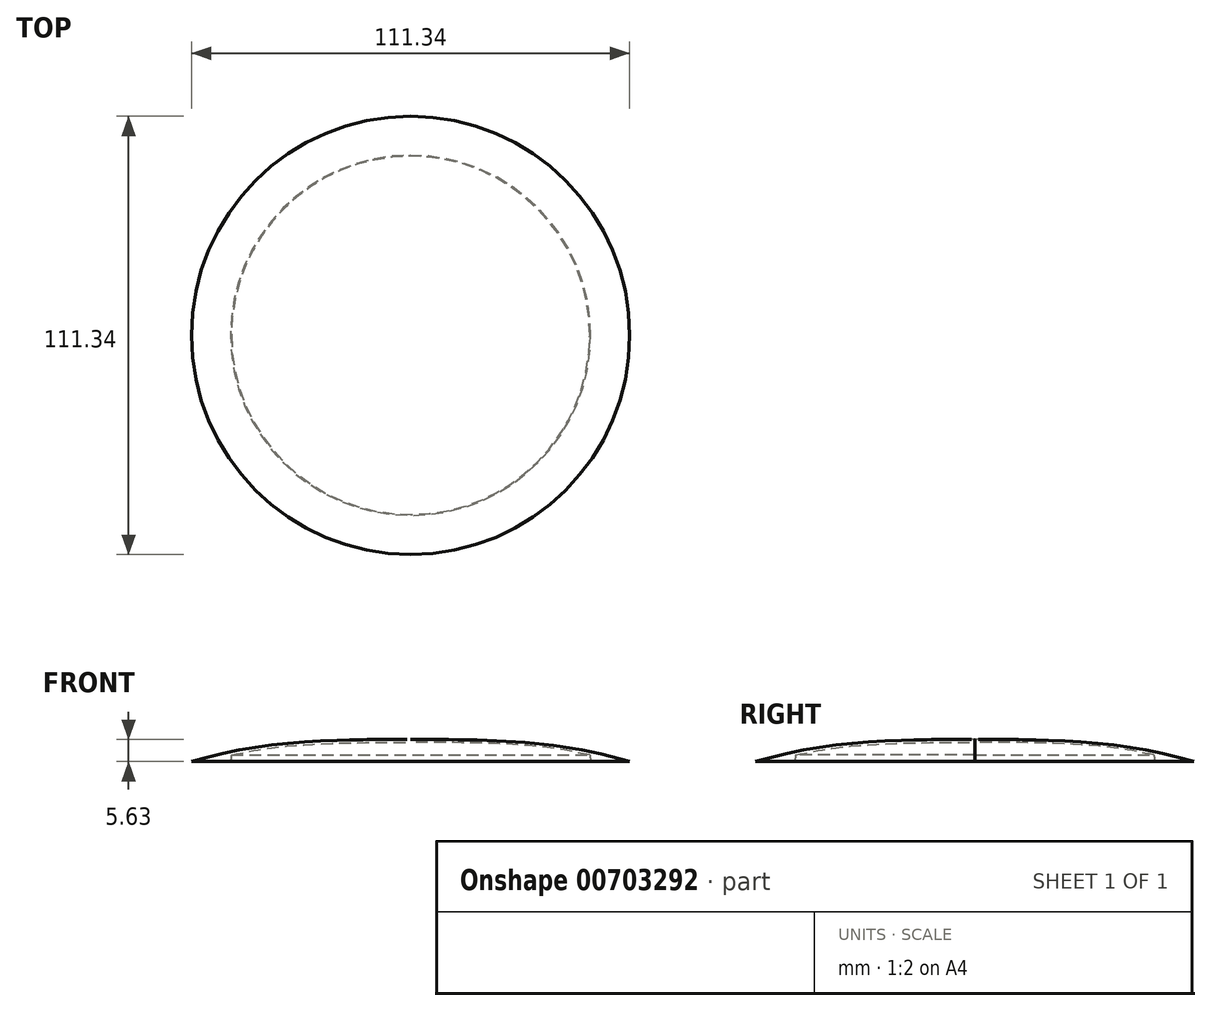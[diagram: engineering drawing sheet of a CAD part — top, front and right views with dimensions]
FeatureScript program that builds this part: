
annotation { "Feature Type Name" : "Feature", "Feature Type Description" : "" }
export const myFeature = defineFeature(function(context is Context, id is Id, definition is map)
    precondition{}
    {
        {
            var Q0;
            Q0=qCreatedBy(makeId("Front.planeOp"),FACE);
            var sketch = newSketch(context, id + "F0", { "sketchPlane" : qUnion([Q0])});
            skFitSpline(sketch, "E0", {"points": [v(-55.4, 0) * mm, v(0, 5.63) * mm, v(55.67, 0) * mm], "startDerivative": vector(110.87, 33.66) * mm, "endDerivative": vector(111.28, -33.63) * mm});
            skLineSegment(sketch, "E1", {"start": v(0, 0) * mm, "end": v(55.67, 0) * mm});
            skLineSegment(sketch, "E2", {"start": v(0, 0) * mm, "end": v(0, 5.63) * mm});
            skArc(sketch, "E3", {"start": v(55.67, 0) * mm, "mid": v(56.17, -0.8) * mm, "end": v(55.45, -1.4) * mm});
            skFitSpline(sketch, "E4", {"points": [v(55.45, -1.4) * mm, v(52.45, -1.64) * mm, v(49.65, -2.13) * mm, v(46.75, -3.08) * mm], "startDerivative": vector(-9.04, -0.6) * mm, "endDerivative": vector(-8.62, -3.09) * mm});
            skArc(sketch, "E5", {"start": v(46.75, -3.08) * mm, "mid": v(46.33, -3.05) * mm, "end": v(46.08, -2.72) * mm});
            skLineSegment(sketch, "E6", {"start": v(46.08, -2.72) * mm, "end": v(45.53, 1.68) * mm});
            skFitSpline(sketch, "E7", {"points": [v(45.53, 1.68) * mm, v(30.7, 4.03) * mm, v(13.33, 4.8) * mm, v(0, 4.91) * mm], "startDerivative": vector(-55.93, 11.67) * mm, "endDerivative": vector(-40.93, 0.2) * mm});
            skSolve(sketch);
        }
        {
            var Q0;
            {var subQ5=sQuery(id+"F0.wireOp",EDGE,"E0");Q0=makeQuery(id+"F0.imprint","IMPRINT",FACE,{"disambiguationData":[TD([[makeQuery(id+"F0.imprint","IMPRINT",EDGE,{"derivedFrom":subQ5}),-1.0]])]});}
            var Q1;
            {var subQ0=sQuery(id+"F0.wireOp",EDGE,"E3");Q1=makeQuery(id+"F0.imprint","IMPRINT",FACE,{"disambiguationData":[TD([[makeQuery(id+"F0.imprint","IMPRINT",EDGE,{"derivedFrom":subQ0}),-1.0]])]});}
            var Q2;
            Q2=sQuery(id+"F0.wireOp",EDGE,"E2");
            revolve(context, id + "F1", {"surfaceOperationType" : NewSurfaceOperationType.NEW, "entities" : qUnion([Q0, Q1]), "axis" : qUnion([Q2]), "revolveType" : RevolveType.FULL});
        }
    });
